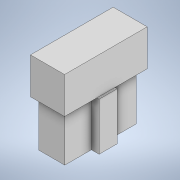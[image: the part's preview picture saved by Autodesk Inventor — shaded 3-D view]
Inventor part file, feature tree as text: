
AUTODESK INVENTOR PART (.ipt)
format: ipt  version: 2020 (Build 240168000, 168)  size: 113,152 bytes
history: native  units: mm
features: extrude x2, sketch x2, other x1
ambient origin geometry x8: Origin, YZ Plane, XZ Plane, XY Plane, X Axis, Y Axis, Z Axis, Center Point
bodies: Body1 (feature_tree)
feature tree (5):
  other  "Bryła1"
  extrude  "Wyciągnięcie proste1"  Depth=15.7mm
  extrude  "Wyciągnięcie proste2"  Depth=5.7mm
  sketch  "Szkic1"
  sketch  "Szkic2"
